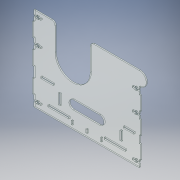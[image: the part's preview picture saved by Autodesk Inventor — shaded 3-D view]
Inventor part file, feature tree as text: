
AUTODESK INVENTOR PART (.ipt)
format: ipt  version: 2019 (Build 230136000, 136)  size: 427,520 bytes
history: native  units: mm
features: extrude x4, sketch x4, fillet x2
ambient origin geometry x8: Origin, YZ Plane, XZ Plane, XY Plane, X Axis, Y Axis, Z Axis, Center Point
bodies: Solid1 (feature_tree)
feature tree (10):
  extrude  "Extrusion1"  Depth=220.0mm
  fillet  "Fillet1"  Radius=300.0mm
  extrude  "Extrusion3"  Depth=100.0mm
  extrude  "Extrusion4"  Depth=3.5mm TaperAngle=0.0deg
  extrude  "Extrusion5"  Depth=3.5mm TaperAngle=0.0deg
  fillet  "Fillet2"  Radius=3.5mm
  sketch  "Sketch1"  dims[d2=300.0mm d3=220.0mm d4=300.0mm]
  sketch  "Sketch4"  dims[d5=20.0mm d6=100.0mm]
  sketch  "Sketch5"  dims[d7=30.0mm d8=3.5mm d9=0.0mm]
  sketch  "Sketch6"  dims[d22=10.0mm d23=40.0mm d24=20.0mm d25=15.0mm d26=3.5mm d27=40.0mm d28=3.5mm d29=40.0mm d30=20.0mm d31=20.0mm d32=3.5mm d33=40.0mm d34=20.0mm d35=3.5mm d36=40.0mm d37=3.5mm d38=40.0mm d39=3.5mm d40=40.0mm d41=30.0mm d42=30.0mm d43=30.0mm d44=3.5mm d45=0.0mm d46=20.0mm d47=4.0mm d48=4.0mm d49=8.0mm d50=8.0mm d51=8.0mm d52=20.0mm d53=4.0mm d54=4.0mm d55=8.0mm d56=8.0mm d57=20.0mm d58=4.0mm d59=4.0mm d60=8.0mm d61=8.0mm d62=8.0mm d63=6.0mm d64=20.0mm d65=8.0mm d66=4.0mm d67=8.0mm d68=13.0mm d69=2.0mm d70=8.0mm d71=4.0mm d72=2.0mm d73=8.0mm d74=4.0mm d75=2.0mm d76=13.0mm d77=13.0mm d78=8.0mm d79=8.0mm d80=3.5mm d81=0.0mm d82=100.0mm d83=25.0mm d84=3.5mm d85=0.0mm d86=12.5mm]
